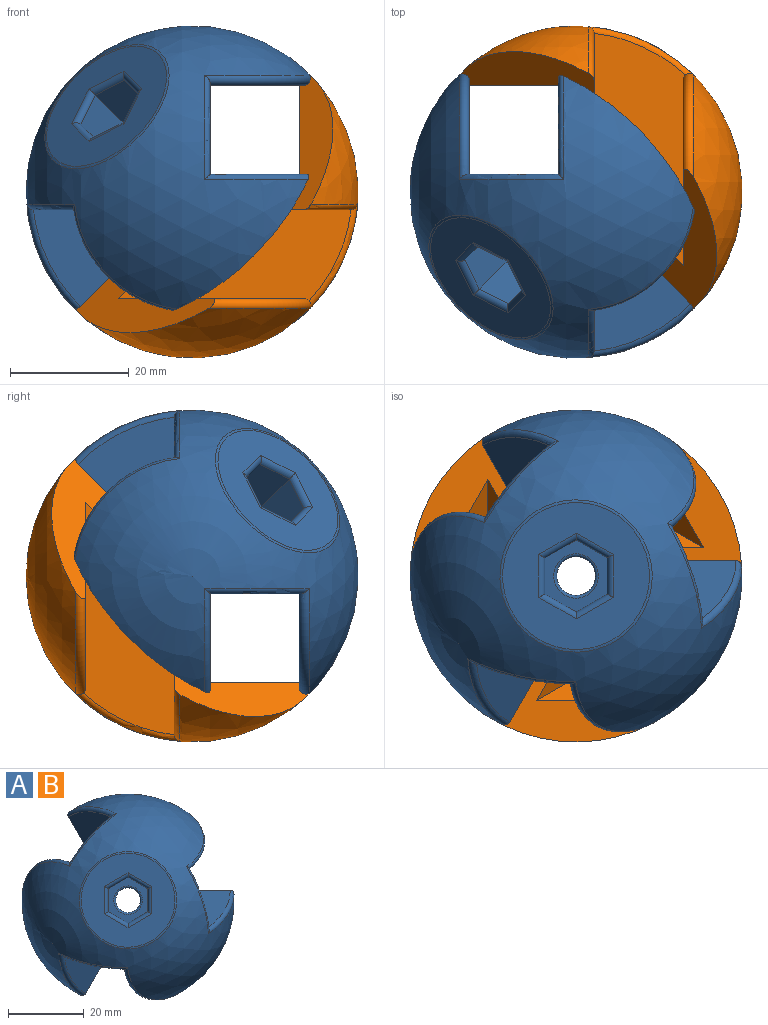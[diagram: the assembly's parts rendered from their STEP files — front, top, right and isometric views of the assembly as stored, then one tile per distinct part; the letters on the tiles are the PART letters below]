
ASSEMBLY  parts=2 mates=3
PART A: 37 faces, bbox 51.8x58.2x58.2 mm
  f0: sphere r=28mm, area 2696.2mm2, adj f7,f20,f21,f22,f23,f24,f25,f26
  f1: plane 10.15x7.67mm, normal (0,0.71,0.71), area 54.6mm2, adj f2,f6,f18,f35
  f2: plane 10.15x7.67mm, normal (-0.71,0.71,0), area 54.6mm2, adj f1,f3,f18,f34
  f3: plane 10.15x7.67mm, normal (-0.71,0,-0.71), area 54.6mm2, adj f2,f4,f18,f32
  f4: plane 10.15x7.67mm, normal (0,-0.71,-0.71), area 54.6mm2, adj f3,f5,f18,f30
  f5: plane 10.15x7.67mm, normal (0.71,-0.71,0), area 54.6mm2, adj f4,f6,f18,f31
  f6: plane 10.15x7.67mm, normal (0.71,0,0.71), area 54.6mm2, adj f1,f5,f18,f33
  f7: plane 43.59x43.59mm, normal (0.58,0.58,-0.58), area 984.9mm2, adj f0,f8,f9,f10,f11,f12,f13,f14
  f8: cylinder r=3.25mm len=12.81mm, axis (-0.58,-0.58,0.58), area 265.5mm2, adj f7,f36
  f9: plane 39.17x15.36mm, normal (1,0,0), area 438.7mm2, adj f7,f10,f11,f23,f25
  f10: plane 24.16x16.24mm, normal (0,0,1), area 215.1mm2, adj f7,f9,f24
  f11: plane 31.35x15.87mm, normal (0,0,-1), area 301.9mm2, adj f7,f9,f23
  f12: plane 24.16x16.24mm, normal (0,-1,0), area 215.1mm2, adj f7,f13,f22
  f13: plane 39.17x15.36mm, normal (0,0,-1), area 438.7mm2, adj f7,f12,f14,f20,f21
  f14: plane 31.35x15.87mm, normal (0,1,0), area 301.9mm2, adj f7,f13,f20
  f15: plane 31.35x15.87mm, normal (1,0,0), area 301.9mm2, adj f7,f16,f28
  f16: plane 39.17x15.36mm, normal (0,1,0), area 438.7mm2, adj f7,f15,f17,f27,f28
  f17: plane 24.16x16.24mm, normal (-1,0,0), area 215.1mm2, adj f7,f16,f26
  f18: plane 9.9x9.9mm, normal (-0.58,-0.58,0.58), area 51.3mm2, adj f1,f2,f3,f4,f5,f6,f36
  f19: plane 20.2x20.2mm, normal (-0.58,-0.58,0.58), area 345.3mm2, adj f29,f30,f31,f32,f33,f34,f35
  f20: torus R=19.18mm, axis (0,-1,0), area 58.7mm2, adj f0,f7,f13,f14,f21
  f21: torus R=26.93mm, axis (0,0,1), area 27.4mm2, adj f0,f13,f20,f22
  f22: torus R=26.93mm, axis (0,-1,0), area 28.5mm2, adj f0,f7,f12,f21
  f23: torus R=19.18mm, axis (0,0,-1), area 58.7mm2, adj f0,f7,f9,f11,f25
  f24: torus R=26.93mm, axis (0,0,-1), area 28.5mm2, adj f0,f7,f10,f25
  f25: torus R=26.93mm, axis (1,0,0), area 27.4mm2, adj f0,f9,f23,f24
  f26: torus R=26.93mm, axis (-1,0,0), area 28.5mm2, adj f0,f7,f17,f27
  f27: torus R=26.93mm, axis (0,-1,0), area 27.4mm2, adj f0,f16,f26,f28
  f28: torus R=19.18mm, axis (-1,0,0), area 58.7mm2, adj f0,f7,f15,f16,f27
  f29: torus R=12.37mm, axis (-0.58,-0.58,0.58), area 37.7mm2, adj f0,f19
  f30: cylinder r=1mm len=6.47mm, axis (-0.82,0.41,-0.41), area 10.2mm2, adj f4,f19,f31,f32
  f31: cylinder r=1mm len=6.47mm, axis (-0.41,-0.41,-0.82), area 10.2mm2, adj f5,f19,f30,f33
  f32: cylinder r=1mm len=6.47mm, axis (-0.41,0.82,0.41), area 10.2mm2, adj f3,f19,f30,f34
  f33: cylinder r=1mm len=6.47mm, axis (0.41,-0.82,-0.41), area 10.2mm2, adj f6,f19,f31,f35
  f34: cylinder r=1mm len=6.47mm, axis (0.41,0.41,0.82), area 10.2mm2, adj f2,f19,f32,f35
  f35: cylinder r=1mm len=6.47mm, axis (0.82,-0.41,0.41), area 10.2mm2, adj f1,f19,f33,f34
  f36: torus R=3.75mm, axis (-0.58,-0.58,0.58), area 16.9mm2, adj f8,f18
PART B: same geometry as A
PLACE A at identity fixed
PLACE B rot(axis=(0.71,-0.71,0),180deg) t=(0,0,0)mm
MATE cylindrical A.f8 <-> B.f8  axis (-0.58,-0.58,0.58) through (-4.62,-4.62,4.62)mm
MATE planar B.f10 <-> A.f13  axis (0,0,-1) through (16.71,-8.68,-3)mm
MATE planar B.f9 <-> A.f12  axis (0,-1,0) through (9.46,-3,-10.86)mm
